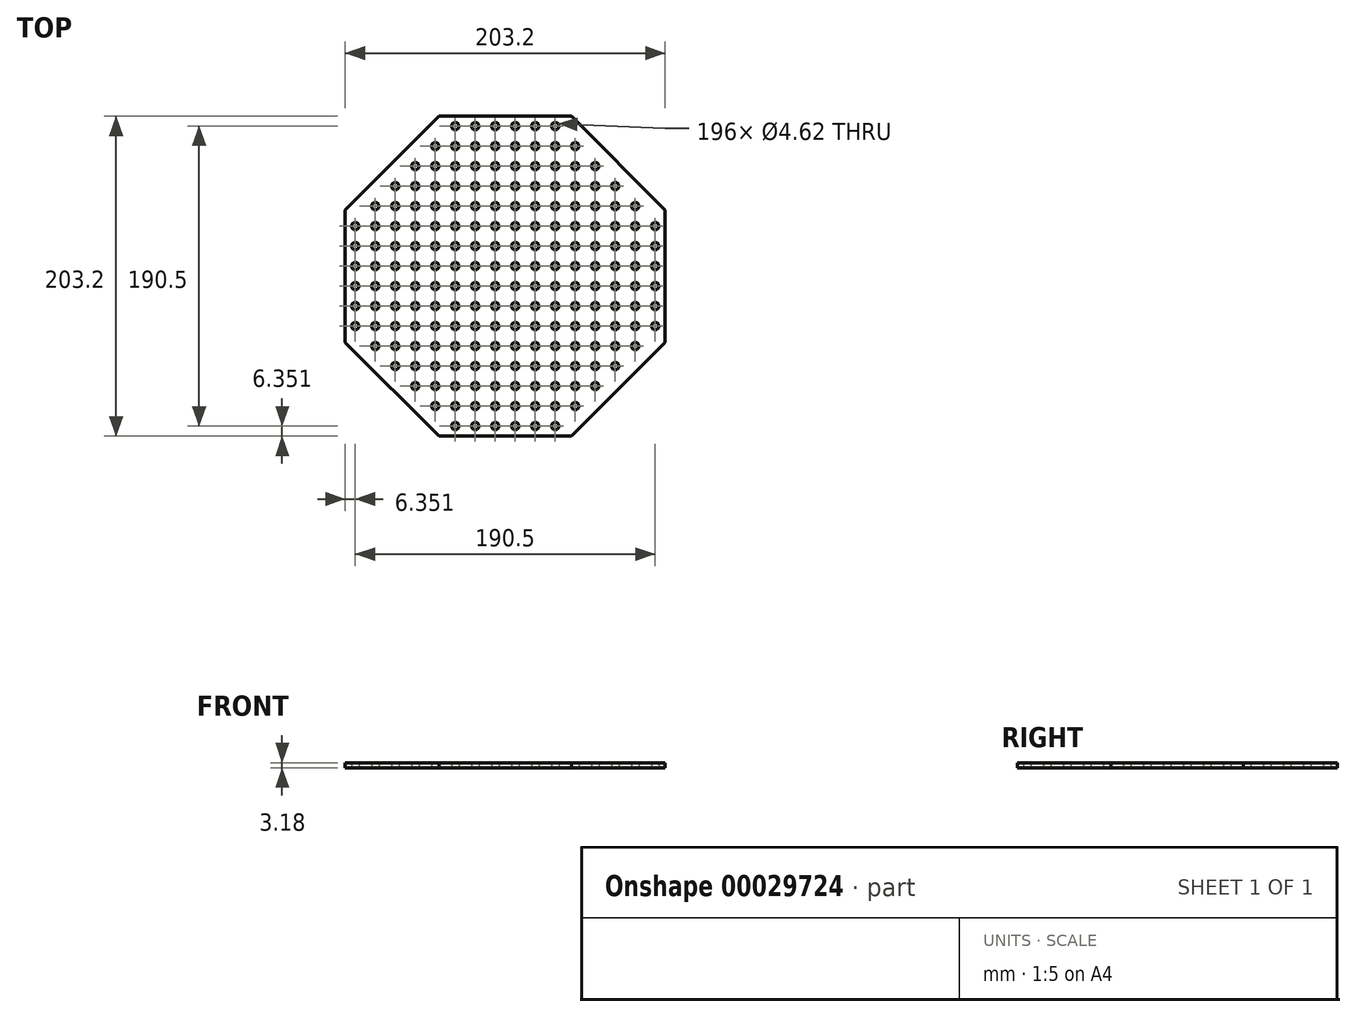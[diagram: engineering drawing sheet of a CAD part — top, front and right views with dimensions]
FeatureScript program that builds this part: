
annotation { "Feature Type Name" : "Feature", "Feature Type Description" : "" }
export const myFeature = defineFeature(function(context is Context, id is Id, definition is map)
    precondition{}
    {
        {
            var Q0;
            Q0=qCreatedBy(makeId("Top.planeOp"),FACE);
            var sketch = newSketch(context, id + "F0", { "sketchPlane" : qUnion([Q0])});
            skLineSegment(sketch, "E0", {"start": v(-159.95, 77.7) * mm, "end": v(-100.43, 137.22) * mm});
            skLineSegment(sketch, "E1", {"start": v(-100.43, 137.22) * mm, "end": v(-16.26, 137.22) * mm});
            skLineSegment(sketch, "E2", {"start": v(-16.26, 137.22) * mm, "end": v(43.25, 77.7) * mm});
            skLineSegment(sketch, "E3", {"start": v(43.25, 77.7) * mm, "end": v(43.25, -6.46) * mm});
            skLineSegment(sketch, "E4", {"start": v(43.25, -6.46) * mm, "end": v(-16.26, -65.98) * mm});
            skLineSegment(sketch, "E5", {"start": v(-16.26, -65.98) * mm, "end": v(-100.43, -65.98) * mm});
            skLineSegment(sketch, "E6", {"start": v(-100.43, -65.98) * mm, "end": v(-159.95, -6.46) * mm});
            skLineSegment(sketch, "E7", {"start": v(-159.95, -6.46) * mm, "end": v(-159.95, 77.7) * mm});
            skCircle(sketch, "E8.0.5.0", {"center": v(-153.6, 67.37) * mm, "radius": 2.31 * mm});
            skCircle(sketch, "E8.0.6.0", {"center": v(-153.6, 54.67) * mm, "radius": 2.31 * mm});
            skCircle(sketch, "E8.0.7.0", {"center": v(-153.6, 41.97) * mm, "radius": 2.31 * mm});
            skCircle(sketch, "E8.0.8.0", {"center": v(-153.6, 29.27) * mm, "radius": 2.31 * mm});
            skCircle(sketch, "E8.0.9.0", {"center": v(-153.6, 16.57) * mm, "radius": 2.31 * mm});
            skCircle(sketch, "E8.0.10.0", {"center": v(-153.6, 3.87) * mm, "radius": 2.31 * mm});
            skCircle(sketch, "E8.1.4.0", {"center": v(-140.9, 80.07) * mm, "radius": 2.31 * mm});
            skCircle(sketch, "E8.1.5.0", {"center": v(-140.9, 67.37) * mm, "radius": 2.31 * mm});
            skCircle(sketch, "E8.1.6.0", {"center": v(-140.9, 54.67) * mm, "radius": 2.31 * mm});
            skCircle(sketch, "E8.1.7.0", {"center": v(-140.9, 41.97) * mm, "radius": 2.31 * mm});
            skCircle(sketch, "E8.1.8.0", {"center": v(-140.9, 29.27) * mm, "radius": 2.31 * mm});
            skCircle(sketch, "E8.1.9.0", {"center": v(-140.9, 16.57) * mm, "radius": 2.31 * mm});
            skCircle(sketch, "E8.1.10.0", {"center": v(-140.9, 3.87) * mm, "radius": 2.31 * mm});
            skCircle(sketch, "E8.1.11.0", {"center": v(-140.9, -8.83) * mm, "radius": 2.31 * mm});
            skCircle(sketch, "E8.2.3.0", {"center": v(-128.2, 92.77) * mm, "radius": 2.31 * mm});
            skCircle(sketch, "E8.2.4.0", {"center": v(-128.2, 80.07) * mm, "radius": 2.31 * mm});
            skCircle(sketch, "E8.2.5.0", {"center": v(-128.2, 67.37) * mm, "radius": 2.31 * mm});
            skCircle(sketch, "E8.2.6.0", {"center": v(-128.2, 54.67) * mm, "radius": 2.31 * mm});
            skCircle(sketch, "E8.2.7.0", {"center": v(-128.2, 41.97) * mm, "radius": 2.31 * mm});
            skCircle(sketch, "E8.2.8.0", {"center": v(-128.2, 29.27) * mm, "radius": 2.31 * mm});
            skCircle(sketch, "E8.2.9.0", {"center": v(-128.2, 16.57) * mm, "radius": 2.31 * mm});
            skCircle(sketch, "E8.2.10.0", {"center": v(-128.2, 3.87) * mm, "radius": 2.31 * mm});
            skCircle(sketch, "E8.2.11.0", {"center": v(-128.2, -8.83) * mm, "radius": 2.31 * mm});
            skCircle(sketch, "E8.2.12.0", {"center": v(-128.2, -21.53) * mm, "radius": 2.31 * mm});
            skCircle(sketch, "E8.3.2.0", {"center": v(-115.5, 105.47) * mm, "radius": 2.31 * mm});
            skCircle(sketch, "E8.3.3.0", {"center": v(-115.5, 92.77) * mm, "radius": 2.31 * mm});
            skCircle(sketch, "E8.3.4.0", {"center": v(-115.5, 80.07) * mm, "radius": 2.31 * mm});
            skCircle(sketch, "E8.3.5.0", {"center": v(-115.5, 67.37) * mm, "radius": 2.31 * mm});
            skCircle(sketch, "E8.3.6.0", {"center": v(-115.5, 54.67) * mm, "radius": 2.31 * mm});
            skCircle(sketch, "E8.3.7.0", {"center": v(-115.5, 41.97) * mm, "radius": 2.31 * mm});
            skCircle(sketch, "E8.3.8.0", {"center": v(-115.5, 29.27) * mm, "radius": 2.31 * mm});
            skCircle(sketch, "E8.3.9.0", {"center": v(-115.5, 16.57) * mm, "radius": 2.31 * mm});
            skCircle(sketch, "E8.3.10.0", {"center": v(-115.5, 3.87) * mm, "radius": 2.31 * mm});
            skCircle(sketch, "E8.3.11.0", {"center": v(-115.5, -8.83) * mm, "radius": 2.31 * mm});
            skCircle(sketch, "E8.3.12.0", {"center": v(-115.5, -21.53) * mm, "radius": 2.31 * mm});
            skCircle(sketch, "E8.3.13.0", {"center": v(-115.5, -34.23) * mm, "radius": 2.31 * mm});
            skCircle(sketch, "E8.4.1.0", {"center": v(-102.8, 118.17) * mm, "radius": 2.31 * mm});
            skCircle(sketch, "E8.4.2.0", {"center": v(-102.8, 105.47) * mm, "radius": 2.31 * mm});
            skCircle(sketch, "E8.4.3.0", {"center": v(-102.8, 92.77) * mm, "radius": 2.31 * mm});
            skCircle(sketch, "E8.4.4.0", {"center": v(-102.8, 80.07) * mm, "radius": 2.31 * mm});
            skCircle(sketch, "E8.4.5.0", {"center": v(-102.8, 67.37) * mm, "radius": 2.31 * mm});
            skCircle(sketch, "E8.4.6.0", {"center": v(-102.8, 54.67) * mm, "radius": 2.31 * mm});
            skCircle(sketch, "E8.4.7.0", {"center": v(-102.8, 41.97) * mm, "radius": 2.31 * mm});
            skCircle(sketch, "E8.4.8.0", {"center": v(-102.8, 29.27) * mm, "radius": 2.31 * mm});
            skCircle(sketch, "E8.4.9.0", {"center": v(-102.8, 16.57) * mm, "radius": 2.31 * mm});
            skCircle(sketch, "E8.4.10.0", {"center": v(-102.8, 3.87) * mm, "radius": 2.31 * mm});
            skCircle(sketch, "E8.4.11.0", {"center": v(-102.8, -8.83) * mm, "radius": 2.31 * mm});
            skCircle(sketch, "E8.4.12.0", {"center": v(-102.8, -21.53) * mm, "radius": 2.31 * mm});
            skCircle(sketch, "E8.4.13.0", {"center": v(-102.8, -34.23) * mm, "radius": 2.31 * mm});
            skCircle(sketch, "E8.4.14.0", {"center": v(-102.8, -46.93) * mm, "radius": 2.31 * mm});
            skCircle(sketch, "E8.5.0.0", {"center": v(-90.1, 130.87) * mm, "radius": 2.31 * mm});
            skCircle(sketch, "E8.5.1.0", {"center": v(-90.1, 118.17) * mm, "radius": 2.31 * mm});
            skCircle(sketch, "E8.5.2.0", {"center": v(-90.1, 105.47) * mm, "radius": 2.31 * mm});
            skCircle(sketch, "E8.5.3.0", {"center": v(-90.1, 92.77) * mm, "radius": 2.31 * mm});
            skCircle(sketch, "E8.5.4.0", {"center": v(-90.1, 80.07) * mm, "radius": 2.31 * mm});
            skCircle(sketch, "E8.5.5.0", {"center": v(-90.1, 67.37) * mm, "radius": 2.31 * mm});
            skCircle(sketch, "E8.5.6.0", {"center": v(-90.1, 54.67) * mm, "radius": 2.31 * mm});
            skCircle(sketch, "E8.5.7.0", {"center": v(-90.1, 41.97) * mm, "radius": 2.31 * mm});
            skCircle(sketch, "E8.5.8.0", {"center": v(-90.1, 29.27) * mm, "radius": 2.31 * mm});
            skCircle(sketch, "E8.5.9.0", {"center": v(-90.1, 16.57) * mm, "radius": 2.31 * mm});
            skCircle(sketch, "E8.5.10.0", {"center": v(-90.1, 3.87) * mm, "radius": 2.31 * mm});
            skCircle(sketch, "E8.5.11.0", {"center": v(-90.1, -8.83) * mm, "radius": 2.31 * mm});
            skCircle(sketch, "E8.5.12.0", {"center": v(-90.1, -21.53) * mm, "radius": 2.31 * mm});
            skCircle(sketch, "E8.5.13.0", {"center": v(-90.1, -34.23) * mm, "radius": 2.31 * mm});
            skCircle(sketch, "E8.5.14.0", {"center": v(-90.1, -46.93) * mm, "radius": 2.31 * mm});
            skCircle(sketch, "E8.5.15.0", {"center": v(-90.1, -59.63) * mm, "radius": 2.31 * mm});
            skCircle(sketch, "E8.6.0.0", {"center": v(-77.4, 130.87) * mm, "radius": 2.31 * mm});
            skCircle(sketch, "E8.6.1.0", {"center": v(-77.4, 118.17) * mm, "radius": 2.31 * mm});
            skCircle(sketch, "E8.6.2.0", {"center": v(-77.4, 105.47) * mm, "radius": 2.31 * mm});
            skCircle(sketch, "E8.6.3.0", {"center": v(-77.4, 92.77) * mm, "radius": 2.31 * mm});
            skCircle(sketch, "E8.6.4.0", {"center": v(-77.4, 80.07) * mm, "radius": 2.31 * mm});
            skCircle(sketch, "E8.6.5.0", {"center": v(-77.4, 67.37) * mm, "radius": 2.31 * mm});
            skCircle(sketch, "E8.6.6.0", {"center": v(-77.4, 54.67) * mm, "radius": 2.31 * mm});
            skCircle(sketch, "E8.6.7.0", {"center": v(-77.4, 41.97) * mm, "radius": 2.31 * mm});
            skCircle(sketch, "E8.6.8.0", {"center": v(-77.4, 29.27) * mm, "radius": 2.31 * mm});
            skCircle(sketch, "E8.6.9.0", {"center": v(-77.4, 16.57) * mm, "radius": 2.31 * mm});
            skCircle(sketch, "E8.6.10.0", {"center": v(-77.4, 3.87) * mm, "radius": 2.31 * mm});
            skCircle(sketch, "E8.6.11.0", {"center": v(-77.4, -8.83) * mm, "radius": 2.31 * mm});
            skCircle(sketch, "E8.6.12.0", {"center": v(-77.4, -21.53) * mm, "radius": 2.31 * mm});
            skCircle(sketch, "E8.6.13.0", {"center": v(-77.4, -34.23) * mm, "radius": 2.31 * mm});
            skCircle(sketch, "E8.6.14.0", {"center": v(-77.4, -46.93) * mm, "radius": 2.31 * mm});
            skCircle(sketch, "E8.6.15.0", {"center": v(-77.4, -59.63) * mm, "radius": 2.31 * mm});
            skCircle(sketch, "E8.7.0.0", {"center": v(-64.7, 130.87) * mm, "radius": 2.31 * mm});
            skCircle(sketch, "E8.7.1.0", {"center": v(-64.7, 118.17) * mm, "radius": 2.31 * mm});
            skCircle(sketch, "E8.7.2.0", {"center": v(-64.7, 105.47) * mm, "radius": 2.31 * mm});
            skCircle(sketch, "E8.7.3.0", {"center": v(-64.7, 92.77) * mm, "radius": 2.31 * mm});
            skCircle(sketch, "E8.7.4.0", {"center": v(-64.7, 80.07) * mm, "radius": 2.31 * mm});
            skCircle(sketch, "E8.7.5.0", {"center": v(-64.7, 67.37) * mm, "radius": 2.31 * mm});
            skCircle(sketch, "E8.7.6.0", {"center": v(-64.7, 54.67) * mm, "radius": 2.31 * mm});
            skCircle(sketch, "E8.7.7.0", {"center": v(-64.7, 41.97) * mm, "radius": 2.31 * mm});
            skCircle(sketch, "E8.7.8.0", {"center": v(-64.7, 29.27) * mm, "radius": 2.31 * mm});
            skCircle(sketch, "E8.7.9.0", {"center": v(-64.7, 16.57) * mm, "radius": 2.31 * mm});
            skCircle(sketch, "E8.7.10.0", {"center": v(-64.7, 3.87) * mm, "radius": 2.31 * mm});
            skCircle(sketch, "E8.7.11.0", {"center": v(-64.7, -8.83) * mm, "radius": 2.31 * mm});
            skCircle(sketch, "E8.7.12.0", {"center": v(-64.7, -21.53) * mm, "radius": 2.31 * mm});
            skCircle(sketch, "E8.7.13.0", {"center": v(-64.7, -34.23) * mm, "radius": 2.31 * mm});
            skCircle(sketch, "E8.7.14.0", {"center": v(-64.7, -46.93) * mm, "radius": 2.31 * mm});
            skCircle(sketch, "E8.7.15.0", {"center": v(-64.7, -59.63) * mm, "radius": 2.31 * mm});
            skCircle(sketch, "E8.8.0.0", {"center": v(-52, 130.87) * mm, "radius": 2.31 * mm});
            skCircle(sketch, "E8.8.1.0", {"center": v(-52, 118.17) * mm, "radius": 2.31 * mm});
            skCircle(sketch, "E8.8.2.0", {"center": v(-52, 105.47) * mm, "radius": 2.31 * mm});
            skCircle(sketch, "E8.8.3.0", {"center": v(-52, 92.77) * mm, "radius": 2.31 * mm});
            skCircle(sketch, "E8.8.4.0", {"center": v(-52, 80.07) * mm, "radius": 2.31 * mm});
            skCircle(sketch, "E8.8.5.0", {"center": v(-52, 67.37) * mm, "radius": 2.31 * mm});
            skCircle(sketch, "E8.8.6.0", {"center": v(-52, 54.67) * mm, "radius": 2.31 * mm});
            skCircle(sketch, "E8.8.7.0", {"center": v(-52, 41.97) * mm, "radius": 2.31 * mm});
            skCircle(sketch, "E8.8.8.0", {"center": v(-52, 29.27) * mm, "radius": 2.31 * mm});
            skCircle(sketch, "E8.8.9.0", {"center": v(-52, 16.57) * mm, "radius": 2.31 * mm});
            skCircle(sketch, "E8.8.10.0", {"center": v(-52, 3.87) * mm, "radius": 2.31 * mm});
            skCircle(sketch, "E8.8.11.0", {"center": v(-52, -8.83) * mm, "radius": 2.31 * mm});
            skCircle(sketch, "E8.8.12.0", {"center": v(-52, -21.53) * mm, "radius": 2.31 * mm});
            skCircle(sketch, "E8.8.13.0", {"center": v(-52, -34.23) * mm, "radius": 2.31 * mm});
            skCircle(sketch, "E8.8.14.0", {"center": v(-52, -46.93) * mm, "radius": 2.31 * mm});
            skCircle(sketch, "E8.8.15.0", {"center": v(-52, -59.63) * mm, "radius": 2.31 * mm});
            skCircle(sketch, "E8.9.0.0", {"center": v(-39.3, 130.87) * mm, "radius": 2.31 * mm});
            skCircle(sketch, "E8.9.1.0", {"center": v(-39.3, 118.17) * mm, "radius": 2.31 * mm});
            skCircle(sketch, "E8.9.2.0", {"center": v(-39.3, 105.47) * mm, "radius": 2.31 * mm});
            skCircle(sketch, "E8.9.3.0", {"center": v(-39.3, 92.77) * mm, "radius": 2.31 * mm});
            skCircle(sketch, "E8.9.4.0", {"center": v(-39.3, 80.07) * mm, "radius": 2.31 * mm});
            skCircle(sketch, "E8.9.5.0", {"center": v(-39.3, 67.37) * mm, "radius": 2.31 * mm});
            skCircle(sketch, "E8.9.6.0", {"center": v(-39.3, 54.67) * mm, "radius": 2.31 * mm});
            skCircle(sketch, "E8.9.7.0", {"center": v(-39.3, 41.97) * mm, "radius": 2.31 * mm});
            skCircle(sketch, "E8.9.8.0", {"center": v(-39.3, 29.27) * mm, "radius": 2.31 * mm});
            skCircle(sketch, "E8.9.9.0", {"center": v(-39.3, 16.57) * mm, "radius": 2.31 * mm});
            skCircle(sketch, "E8.9.10.0", {"center": v(-39.3, 3.87) * mm, "radius": 2.31 * mm});
            skCircle(sketch, "E8.9.11.0", {"center": v(-39.3, -8.83) * mm, "radius": 2.31 * mm});
            skCircle(sketch, "E8.9.12.0", {"center": v(-39.3, -21.53) * mm, "radius": 2.31 * mm});
            skCircle(sketch, "E8.9.13.0", {"center": v(-39.3, -34.23) * mm, "radius": 2.31 * mm});
            skCircle(sketch, "E8.9.14.0", {"center": v(-39.3, -46.93) * mm, "radius": 2.31 * mm});
            skCircle(sketch, "E8.9.15.0", {"center": v(-39.3, -59.63) * mm, "radius": 2.31 * mm});
            skCircle(sketch, "E8.10.0.0", {"center": v(-26.6, 130.87) * mm, "radius": 2.31 * mm});
            skCircle(sketch, "E8.10.1.0", {"center": v(-26.6, 118.17) * mm, "radius": 2.31 * mm});
            skCircle(sketch, "E8.10.2.0", {"center": v(-26.6, 105.47) * mm, "radius": 2.31 * mm});
            skCircle(sketch, "E8.10.3.0", {"center": v(-26.6, 92.77) * mm, "radius": 2.31 * mm});
            skCircle(sketch, "E8.10.4.0", {"center": v(-26.6, 80.07) * mm, "radius": 2.31 * mm});
            skCircle(sketch, "E8.10.5.0", {"center": v(-26.6, 67.37) * mm, "radius": 2.31 * mm});
            skCircle(sketch, "E8.10.6.0", {"center": v(-26.6, 54.67) * mm, "radius": 2.31 * mm});
            skCircle(sketch, "E8.10.7.0", {"center": v(-26.6, 41.97) * mm, "radius": 2.31 * mm});
            skCircle(sketch, "E8.10.8.0", {"center": v(-26.6, 29.27) * mm, "radius": 2.31 * mm});
            skCircle(sketch, "E8.10.9.0", {"center": v(-26.6, 16.57) * mm, "radius": 2.31 * mm});
            skCircle(sketch, "E8.10.10.0", {"center": v(-26.6, 3.87) * mm, "radius": 2.31 * mm});
            skCircle(sketch, "E8.10.11.0", {"center": v(-26.6, -8.83) * mm, "radius": 2.31 * mm});
            skCircle(sketch, "E8.10.12.0", {"center": v(-26.6, -21.53) * mm, "radius": 2.31 * mm});
            skCircle(sketch, "E8.10.13.0", {"center": v(-26.6, -34.23) * mm, "radius": 2.31 * mm});
            skCircle(sketch, "E8.10.14.0", {"center": v(-26.6, -46.93) * mm, "radius": 2.31 * mm});
            skCircle(sketch, "E8.10.15.0", {"center": v(-26.6, -59.63) * mm, "radius": 2.31 * mm});
            skCircle(sketch, "E8.11.1.0", {"center": v(-13.9, 118.17) * mm, "radius": 2.31 * mm});
            skCircle(sketch, "E8.11.2.0", {"center": v(-13.9, 105.47) * mm, "radius": 2.31 * mm});
            skCircle(sketch, "E8.11.3.0", {"center": v(-13.9, 92.77) * mm, "radius": 2.31 * mm});
            skCircle(sketch, "E8.11.4.0", {"center": v(-13.9, 80.07) * mm, "radius": 2.31 * mm});
            skCircle(sketch, "E8.11.5.0", {"center": v(-13.9, 67.37) * mm, "radius": 2.31 * mm});
            skCircle(sketch, "E8.11.6.0", {"center": v(-13.9, 54.67) * mm, "radius": 2.31 * mm});
            skCircle(sketch, "E8.11.7.0", {"center": v(-13.9, 41.97) * mm, "radius": 2.31 * mm});
            skCircle(sketch, "E8.11.8.0", {"center": v(-13.9, 29.27) * mm, "radius": 2.31 * mm});
            skCircle(sketch, "E8.11.9.0", {"center": v(-13.9, 16.57) * mm, "radius": 2.31 * mm});
            skCircle(sketch, "E8.11.10.0", {"center": v(-13.9, 3.87) * mm, "radius": 2.31 * mm});
            skCircle(sketch, "E8.11.11.0", {"center": v(-13.9, -8.83) * mm, "radius": 2.31 * mm});
            skCircle(sketch, "E8.11.12.0", {"center": v(-13.9, -21.53) * mm, "radius": 2.31 * mm});
            skCircle(sketch, "E8.11.13.0", {"center": v(-13.9, -34.23) * mm, "radius": 2.31 * mm});
            skCircle(sketch, "E8.11.14.0", {"center": v(-13.9, -46.93) * mm, "radius": 2.31 * mm});
            skCircle(sketch, "E8.12.2.0", {"center": v(-1.2, 105.47) * mm, "radius": 2.31 * mm});
            skCircle(sketch, "E8.12.3.0", {"center": v(-1.2, 92.77) * mm, "radius": 2.31 * mm});
            skCircle(sketch, "E8.12.4.0", {"center": v(-1.2, 80.07) * mm, "radius": 2.31 * mm});
            skCircle(sketch, "E8.12.5.0", {"center": v(-1.2, 67.37) * mm, "radius": 2.31 * mm});
            skCircle(sketch, "E8.12.6.0", {"center": v(-1.2, 54.67) * mm, "radius": 2.31 * mm});
            skCircle(sketch, "E8.12.7.0", {"center": v(-1.2, 41.97) * mm, "radius": 2.31 * mm});
            skCircle(sketch, "E8.12.8.0", {"center": v(-1.2, 29.27) * mm, "radius": 2.31 * mm});
            skCircle(sketch, "E8.12.9.0", {"center": v(-1.2, 16.57) * mm, "radius": 2.31 * mm});
            skCircle(sketch, "E8.12.10.0", {"center": v(-1.2, 3.87) * mm, "radius": 2.31 * mm});
            skCircle(sketch, "E8.12.11.0", {"center": v(-1.2, -8.83) * mm, "radius": 2.31 * mm});
            skCircle(sketch, "E8.12.12.0", {"center": v(-1.2, -21.53) * mm, "radius": 2.31 * mm});
            skCircle(sketch, "E8.12.13.0", {"center": v(-1.2, -34.23) * mm, "radius": 2.31 * mm});
            skCircle(sketch, "E8.13.3.0", {"center": v(11.5, 92.77) * mm, "radius": 2.31 * mm});
            skCircle(sketch, "E8.13.4.0", {"center": v(11.5, 80.07) * mm, "radius": 2.31 * mm});
            skCircle(sketch, "E8.13.5.0", {"center": v(11.5, 67.37) * mm, "radius": 2.31 * mm});
            skCircle(sketch, "E8.13.6.0", {"center": v(11.5, 54.67) * mm, "radius": 2.31 * mm});
            skCircle(sketch, "E8.13.7.0", {"center": v(11.5, 41.97) * mm, "radius": 2.31 * mm});
            skCircle(sketch, "E8.13.8.0", {"center": v(11.5, 29.27) * mm, "radius": 2.31 * mm});
            skCircle(sketch, "E8.13.9.0", {"center": v(11.5, 16.57) * mm, "radius": 2.31 * mm});
            skCircle(sketch, "E8.13.10.0", {"center": v(11.5, 3.87) * mm, "radius": 2.31 * mm});
            skCircle(sketch, "E8.13.11.0", {"center": v(11.5, -8.83) * mm, "radius": 2.31 * mm});
            skCircle(sketch, "E8.13.12.0", {"center": v(11.5, -21.53) * mm, "radius": 2.31 * mm});
            skCircle(sketch, "E8.14.4.0", {"center": v(24.2, 80.07) * mm, "radius": 2.31 * mm});
            skCircle(sketch, "E8.14.5.0", {"center": v(24.2, 67.37) * mm, "radius": 2.31 * mm});
            skCircle(sketch, "E8.14.6.0", {"center": v(24.2, 54.67) * mm, "radius": 2.31 * mm});
            skCircle(sketch, "E8.14.7.0", {"center": v(24.2, 41.97) * mm, "radius": 2.31 * mm});
            skCircle(sketch, "E8.14.8.0", {"center": v(24.2, 29.27) * mm, "radius": 2.31 * mm});
            skCircle(sketch, "E8.14.9.0", {"center": v(24.2, 16.57) * mm, "radius": 2.31 * mm});
            skCircle(sketch, "E8.14.10.0", {"center": v(24.2, 3.87) * mm, "radius": 2.31 * mm});
            skCircle(sketch, "E8.14.11.0", {"center": v(24.2, -8.83) * mm, "radius": 2.31 * mm});
            skCircle(sketch, "E8.15.5.0", {"center": v(36.9, 67.37) * mm, "radius": 2.31 * mm});
            skCircle(sketch, "E8.15.6.0", {"center": v(36.9, 54.67) * mm, "radius": 2.31 * mm});
            skCircle(sketch, "E8.15.7.0", {"center": v(36.9, 41.97) * mm, "radius": 2.31 * mm});
            skCircle(sketch, "E8.15.8.0", {"center": v(36.9, 29.27) * mm, "radius": 2.31 * mm});
            skCircle(sketch, "E8.15.9.0", {"center": v(36.9, 16.57) * mm, "radius": 2.31 * mm});
            skCircle(sketch, "E8.15.10.0", {"center": v(36.9, 3.87) * mm, "radius": 2.31 * mm});
            skSolve(sketch);
        }
        {
            var Q0;
            Q0=makeQuery(id+"F0.imprint","IMPRINT",FACE,{"disambiguationData":[TD([[makeQuery(id+"F0.imprint","IMPRINT",EDGE,{"derivedFrom":sQuery(id+"F0.wireOp",EDGE,"E0")}),-1.0]])]});
            extrude(context, id + "F1", {"entities" : qUnion([Q0]), "depth" : 3.17 * mm});
        }
    });
